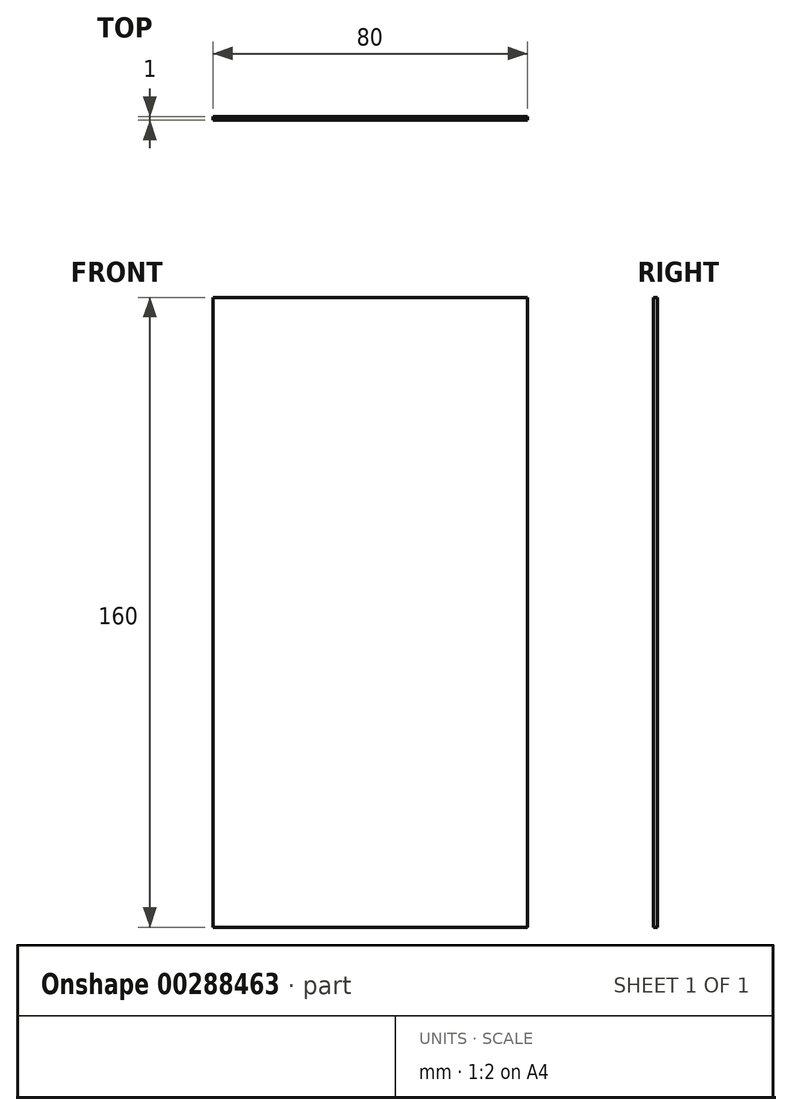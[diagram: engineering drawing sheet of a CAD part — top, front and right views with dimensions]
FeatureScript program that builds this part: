
annotation { "Feature Type Name" : "Feature", "Feature Type Description" : "" }
export const myFeature = defineFeature(function(context is Context, id is Id, definition is map)
    precondition{}
    {
        {
            var Q0;
            Q0=qCreatedBy(makeId("Front.planeOp"),FACE);
            var sketch = newSketch(context, id + "F0", { "sketchPlane" : qUnion([Q0])});
            skLineSegment(sketch, "E0.bottom", {"start": v(-59.5, 131.87) * mm, "end": v(20.5, 131.87) * mm});
            skLineSegment(sketch, "E0.top", {"start": v(-59.5, -28.13) * mm, "end": v(20.5, -28.13) * mm});
            skLineSegment(sketch, "E0.left", {"start": v(-59.5, 131.87) * mm, "end": v(-59.5, -28.13) * mm});
            skLineSegment(sketch, "E0.right", {"start": v(20.5, 131.87) * mm, "end": v(20.5, -28.13) * mm});
            skSolve(sketch);
        }
        {
            var Q0;
            Q0=makeQuery(id+"F0.imprint","IMPRINT",FACE,{"disambiguationData":[TD([[makeQuery(id+"F0.imprint","IMPRINT",EDGE,{"derivedFrom":sQuery(id+"F0.wireOp",EDGE,"E0.bottom")}),-1.0]])]});
            extrude(context, id + "F1", {"entities" : qUnion([Q0]), "depth" : 1 * mm});
        }
    });
